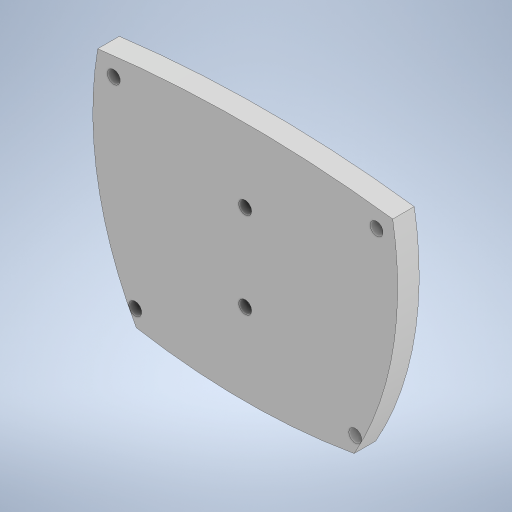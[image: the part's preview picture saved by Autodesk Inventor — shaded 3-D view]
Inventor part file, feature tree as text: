
AUTODESK INVENTOR PART (.ipt)
format: ipt  version: 2023 (Build 270158000, 158)  size: 266,752 bytes
history: native  units: in
note: dims shown in document units (in); Inventor stores cm internally (conversion verified against a paired STEP export)
features: extrude x4, sketch x2
ambient origin geometry x8: Origin, YZ Plane, XZ Plane, XY Plane, X Axis, Y Axis, Z Axis, Center Point
bodies: Solid1 (feature_tree)
feature tree (6):
  sketch  "Sketch1"  dims[d0=0.9055in d1=0.9843in]
  extrude  "Extrusion1"  Depth=0.9843in
  extrude  "Extrusion2"  Depth=1.8898in
  extrude  "Extrusion3"  Depth=0.3937in
  extrude  "Extrusion4"  Depth=0.3937in
  sketch  "Sketch2"  dims[d4=2.5591in d6=1.8898in d7=1.2795in d8=1.2795in d9=0.0787in d10=0.0787in d11=0.0787in d12=0.0787in d13=0.0787in d14=0.1181in d15=0.1969in d16=0.1969in d17=0.0776in d18=0.1461in d19=0.0678in d20=0.1181in d21=0.0787in d22=0.0in d23=0.1181in d24=0.0in d27=0.1181in d28=0.1181in d29=0.1181in d30=0.0in d31=0.3937in d32=0.0in]
